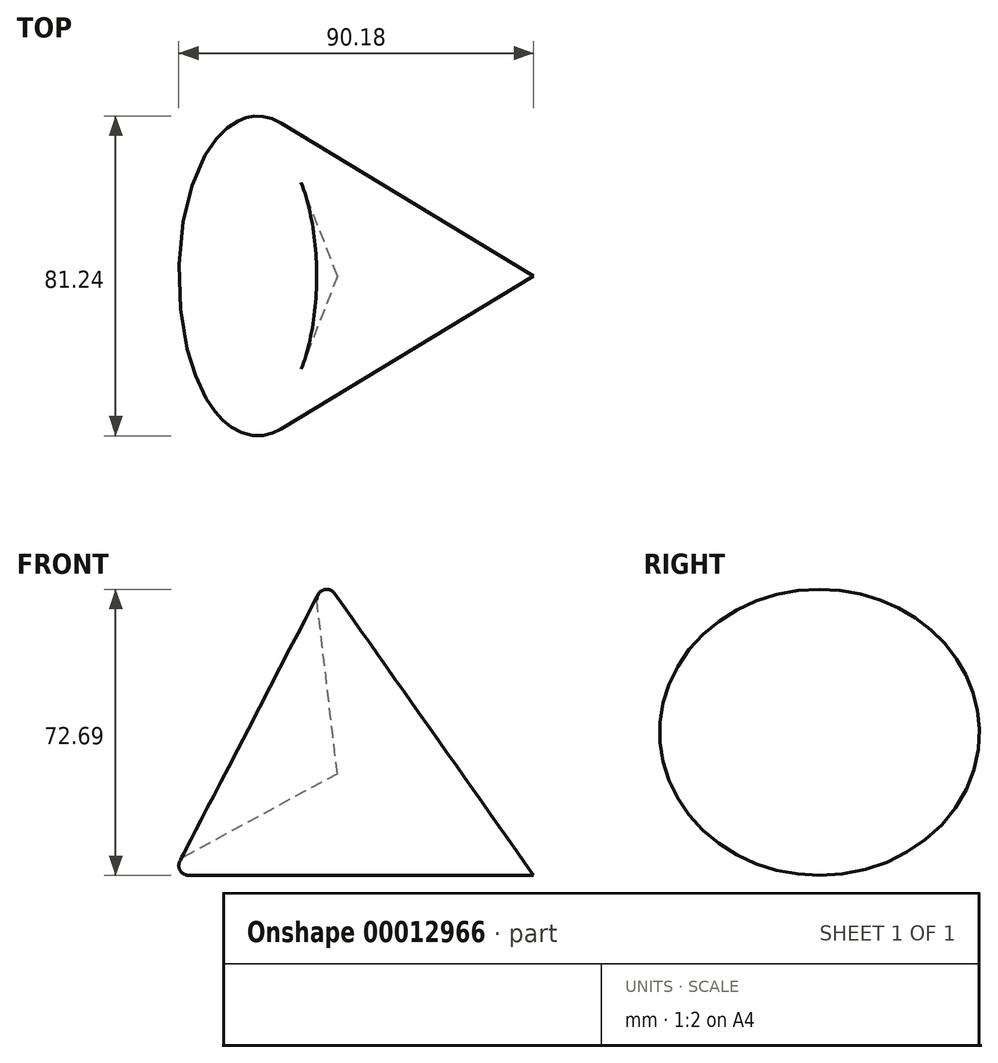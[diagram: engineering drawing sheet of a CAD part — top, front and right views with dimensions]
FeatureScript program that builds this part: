
annotation { "Feature Type Name" : "Feature", "Feature Type Description" : "" }
export const myFeature = defineFeature(function(context is Context, id is Id, definition is map)
    precondition{}
    {
        {
            var Q0;
            Q0=qCreatedBy(makeId("Front.planeOp"),FACE);
            var sketch = newSketch(context, id + "F0", { "sketchPlane" : qUnion([Q0])});
            skLineSegment(sketch, "E0", {"start": v(-47.67, 0) * mm, "end": v(49.87, 0) * mm});
            skLineSegment(sketch, "E1", {"start": v(49.87, 0) * mm, "end": v(0, 25.84) * mm});
            skLineSegment(sketch, "E2", {"start": v(0, 25.84) * mm, "end": v(-47.67, 0) * mm});
            skSolve(sketch);
        }
        {
            var Q0;
            Q0=makeQuery(id+"F0.imprint","IMPRINT",FACE,{"disambiguationData":[TD([[makeQuery(id+"F0.imprint","IMPRINT",EDGE,{"derivedFrom":sQuery(id+"F0.wireOp",EDGE,"E0")}),1.0]])]});
            var Q1;
            Q1=sQuery(id+"F0.wireOp",EDGE,"E1");
            revolve(context, id + "F1", {"entities" : qUnion([Q0]), "axis" : qUnion([Q1]), "revolveType" : RevolveType.FULL});
        }
        {
            var Q0;
            Q0=makeQuery(id+"F1.opRevolve","SWEPT_EDGE",EDGE,{"disambiguationData":[OSD([sQuery(id+"F0.wireOp",EDGE,"E0"),sQuery(id+"F0.wireOp",EDGE,"E2")])]});
            fillet(context, id + "F2", {"entities" : qUnion([Q0]), "radius" : 2.5 * mm, "tangentPropagation" : true, "allowEdgeOverflow" : false});
        }
    });
